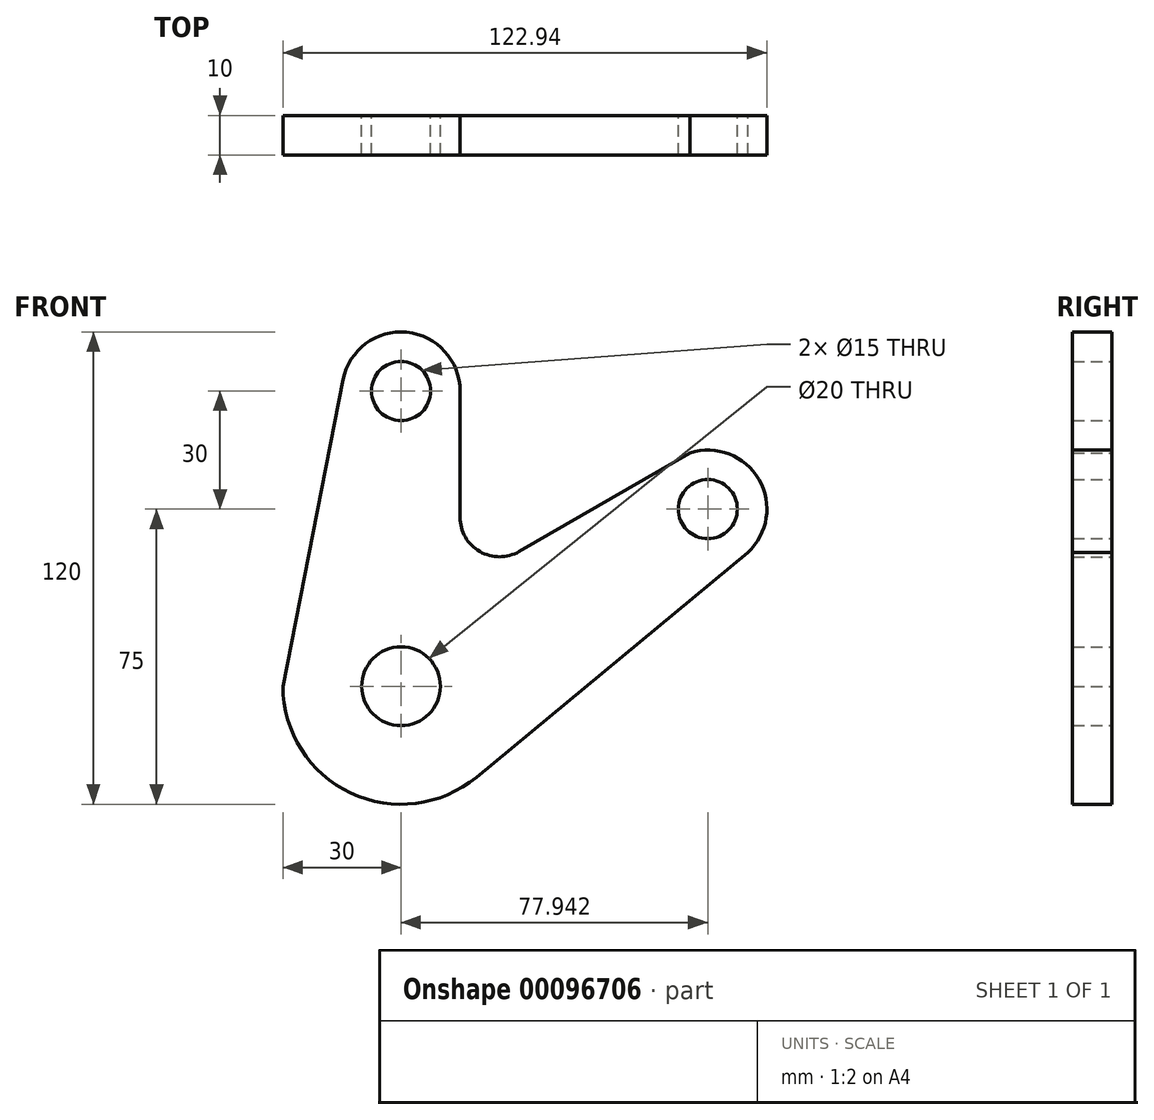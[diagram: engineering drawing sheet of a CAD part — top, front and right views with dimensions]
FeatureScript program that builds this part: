
annotation { "Feature Type Name" : "Feature", "Feature Type Description" : "" }
export const myFeature = defineFeature(function(context is Context, id is Id, definition is map)
    precondition{}
    {
        {
            var Q0;
            Q0=qCreatedBy(makeId("Front.planeOp"),FACE);
            var sketch = newSketch(context, id + "F0", { "sketchPlane" : qUnion([Q0])});
            skCircle(sketch, "E0", {"center": v(0, 0) * mm, "radius": 10 * mm});
            skCircle(sketch, "E1", {"center": v(0, 75) * mm, "radius": 7.5 * mm});
            skCircle(sketch, "E2", {"center": v(77.94, 45) * mm, "radius": 7.5 * mm});
            skLineSegment(sketch, "E3", {"start": v(0, 75) * mm, "end": v(0, 0) * mm, "construction": true});
            skLineSegment(sketch, "E4", {"start": v(77.94, 45) * mm, "end": v(0, 0) * mm, "construction": true});
            skLineSegment(sketch, "E5", {"start": v(15, 42.88) * mm, "end": v(15, 75) * mm});
            skLineSegment(sketch, "E6", {"start": v(-30, 0) * mm, "end": v(-14.72, 77.89) * mm});
            skLineSegment(sketch, "E7", {"start": v(19.13, -23.11) * mm, "end": v(88.1, 33.96) * mm});
            skLineSegment(sketch, "E8", {"start": v(30, 34.22) * mm, "end": v(73.46, 59.31) * mm});
            skArc(sketch, "E9", {"start": v(15, 42.88) * mm, "mid": v(20, 34.22) * mm, "end": v(30, 34.22) * mm});
            skArc(sketch, "E10", {"start": v(15, 75) * mm, "mid": v(1.45, 89.93) * mm, "end": v(-14.72, 77.89) * mm});
            skArc(sketch, "E11", {"start": v(-30, 0) * mm, "mid": v(-12.77, -27.15) * mm, "end": v(19.13, -23.11) * mm});
            skArc(sketch, "E12", {"start": v(88.1, 33.96) * mm, "mid": v(90.93, 52.5) * mm, "end": v(73.46, 59.31) * mm});
            skSolve(sketch);
        }
        {
            var Q0;
            Q0 = qSketchRegion(id + "F0", true);
            extrude(context, id + "F1", {"entities" : qUnion([Q0]), "depth" : 10 * mm});
        }
    });
